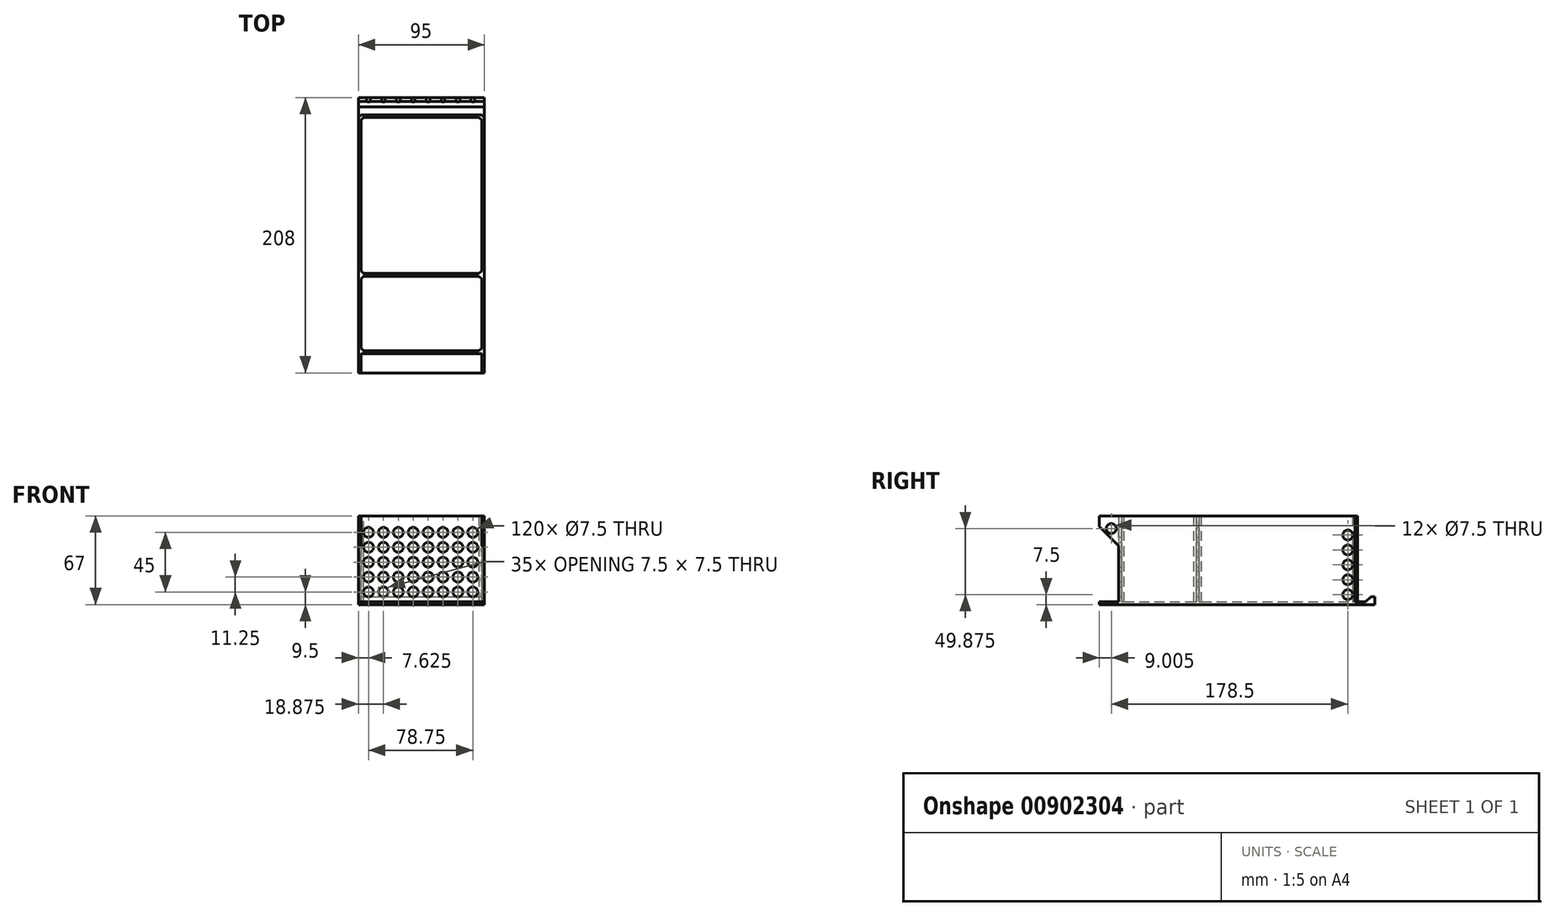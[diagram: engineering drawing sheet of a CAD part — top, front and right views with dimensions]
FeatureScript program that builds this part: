
annotation { "Feature Type Name" : "Feature", "Feature Type Description" : "" }
export const myFeature = defineFeature(function(context is Context, id is Id, definition is map)
    precondition{}
    {
        {
            assignVariable(context, id + "F0", {"name" : "d", "anyValue" : 67});
        }
        {
            assignVariable(context, id + "F1", {"name" : "noz", "anyValue" : .5});
        }
        {
            assignVariable(context, id + "F2", {"name" : "shell", "anyValue" : 2});
        }
        {
            assignVariable(context, id + "F3", {"name" : "wall", "anyValue" : getVariable(context, 'noz') * getVariable(context, 'shell') * 2});
        }
        {
            var Q0;
            Q0=qCreatedBy(makeId("Top.planeOp"),FACE);
            var sketch = newSketch(context, id + "F4", { "sketchPlane" : qUnion([Q0])});
            skLineSegment(sketch, "E0.bottom", {"start": v(0, 174.82) * mm, "end": v(47.5, 174.82) * mm});
            skLineSegment(sketch, "E0.top", {"start": v(0, -11.82) * mm, "end": v(45.5, -11.82) * mm});
            skLineSegment(sketch, "E0.left", {"start": v(0, 172.82) * mm, "end": v(0, -11.82) * mm});
            skLineSegment(sketch, "E0.right", {"start": v(47.5, 174.82) * mm, "end": v(47.5, -11.82) * mm});
            skLineSegment(sketch, "E1", {"start": v(45.5, 172.82) * mm, "end": v(45.5, 54.95) * mm});
            skLineSegment(sketch, "E2.top", {"start": v(47.5, -20.18) * mm, "end": v(45.5, -20.18) * mm});
            skLineSegment(sketch, "E2.left", {"start": v(47.5, -11.82) * mm, "end": v(47.5, -20.18) * mm});
            skLineSegment(sketch, "E2.right", {"start": v(45.5, -5.55) * mm, "end": v(45.5, -20.18) * mm});
            skLineSegment(sketch, "E3.bottom", {"start": v(0, -3.55) * mm, "end": v(45.5, -3.55) * mm});
            skLineSegment(sketch, "E3.top", {"start": v(0, -5.55) * mm, "end": v(45.5, -5.55) * mm});
            skLineSegment(sketch, "E3.left", {"start": v(0, -3.55) * mm, "end": v(0, -5.55) * mm});
            skLineSegment(sketch, "E4.bottom", {"start": v(0, 54.95) * mm, "end": v(45.5, 54.95) * mm});
            skLineSegment(sketch, "E4.top", {"start": v(0, 52.95) * mm, "end": v(45.5, 52.95) * mm});
            skLineSegment(sketch, "E4.left", {"start": v(0, 54.95) * mm, "end": v(0, 52.95) * mm});
            skLineSegment(sketch, "E5.bottom", {"start": v(0, 174.82) * mm, "end": v(48, 174.82) * mm});
            skLineSegment(sketch, "E5.top", {"start": v(0, 172.82) * mm, "end": v(45.5, 172.82) * mm});
            skLineSegment(sketch, "E6.MirrorCS", {"start": v(0, -11.82) * mm, "end": v(-45.5, -11.82) * mm});
            skLineSegment(sketch, "E7.MirrorCS", {"start": v(-47.5, -11.82) * mm, "end": v(-47.5, -20.18) * mm});
            skLineSegment(sketch, "E8.MirrorCS", {"start": v(0, 174.82) * mm, "end": v(-47.5, 174.82) * mm});
            skLineSegment(sketch, "E9.MirrorCS", {"start": v(0, 174.82) * mm, "end": v(-48, 174.82) * mm});
            skLineSegment(sketch, "E10.MirrorCS", {"start": v(-45.5, 172.82) * mm, "end": v(-45.5, 54.95) * mm});
            skLineSegment(sketch, "E11.MirrorCS", {"start": v(-45.5, -5.55) * mm, "end": v(-45.5, -20.18) * mm});
            skLineSegment(sketch, "E12.MirrorCS", {"start": v(0, 172.82) * mm, "end": v(-45.5, 172.82) * mm});
            skLineSegment(sketch, "E13.MirrorCS", {"start": v(-47.5, -20.18) * mm, "end": v(-45.5, -20.18) * mm});
            skLineSegment(sketch, "E14.MirrorCS", {"start": v(0, -3.55) * mm, "end": v(-45.5, -3.55) * mm});
            skLineSegment(sketch, "E15.MirrorCS", {"start": v(0, -5.55) * mm, "end": v(-45.5, -5.55) * mm});
            skLineSegment(sketch, "E16.MirrorCS", {"start": v(-47.5, 174.82) * mm, "end": v(-47.5, -11.82) * mm});
            skLineSegment(sketch, "E17.MirrorCS", {"start": v(0, 54.95) * mm, "end": v(-45.5, 54.95) * mm});
            skLineSegment(sketch, "E18.MirrorCS", {"start": v(0, 52.95) * mm, "end": v(-45.5, 52.95) * mm});
            skPoint(sketch, "E19.orphan", {"position": v(-45.5, 174.82) * mm});
            skPoint(sketch, "E20.orphan", {"position": v(45.5, 174.82) * mm});
            skLineSegment(sketch, "E21.trimOffspring", {"start": v(45.5, 52.95) * mm, "end": v(45.5, -3.55) * mm});
            skLineSegment(sketch, "E22.trimOffspring", {"start": v(-45.5, 52.95) * mm, "end": v(-45.5, -3.55) * mm});
            skPoint(sketch, "E23.orphan", {"position": v(-45.5, -11.82) * mm});
            skPoint(sketch, "E24.orphan", {"position": v(45.5, -11.82) * mm});
            skLineSegment(sketch, "E25", {"start": v(48.56, -20.18) * mm, "end": v(-45.5, -20.18) * mm});
            skLineSegment(sketch, "E26.bottom", {"start": v(-47.5, 174.82) * mm, "end": v(47.5, 174.82) * mm});
            skLineSegment(sketch, "E26.top", {"start": v(-47.5, 187.82) * mm, "end": v(47.5, 187.82) * mm});
            skLineSegment(sketch, "E26.left", {"start": v(-47.5, 174.82) * mm, "end": v(-47.5, 187.82) * mm});
            skLineSegment(sketch, "E26.right", {"start": v(47.5, 174.82) * mm, "end": v(47.5, 187.82) * mm});
            skLineSegment(sketch, "E27", {"start": v(-47.5, 185.82) * mm, "end": v(47.5, 185.82) * mm});
            skLineSegment(sketch, "E28.bottom", {"start": v(-45.5, 157.82) * mm, "end": v(45.5, 157.82) * mm});
            skLineSegment(sketch, "E28.top", {"start": v(-45.5, 155.82) * mm, "end": v(45.5, 155.82) * mm});
            skLineSegment(sketch, "E28.left", {"start": v(-45.5, 157.82) * mm, "end": v(-45.5, 155.82) * mm});
            skLineSegment(sketch, "E28.right", {"start": v(45.5, 157.82) * mm, "end": v(45.5, 155.82) * mm});
            skLineSegment(sketch, "E29.bottom", {"start": v(-45.5, 92.57) * mm, "end": v(45.5, 92.57) * mm});
            skLineSegment(sketch, "E29.top", {"start": v(-45.5, 90.57) * mm, "end": v(45.5, 90.57) * mm});
            skLineSegment(sketch, "E29.left", {"start": v(-45.5, 92.57) * mm, "end": v(-45.5, 90.57) * mm});
            skLineSegment(sketch, "E29.right", {"start": v(45.5, 92.57) * mm, "end": v(45.5, 90.57) * mm});
            skSolve(sketch);
        }
        {
            var Q0;
            Q0=makeQuery(id+"F4.imprint","IMPRINT",FACE,{"disambiguationData":[TD([[makeQuery(id+"F4.imprint","IMPRINT",EDGE,{"derivedFrom":sQuery(id+"F4.wireOp",EDGE,"E26.top")}),-1.0]])]});
            var Q1;
            {var subQ7=sQuery(id+"F4.wireOp",EDGE,"E0.right");Q1=makeQuery(id+"F4.imprint","IMPRINT",FACE,{"disambiguationData":[TD([[makeQuery(id+"F4.imprint","IMPRINT",EDGE,{"derivedFrom":subQ7}),-1.0]])]});}
            var Q2;
            Q2=makeQuery(id+"F4.imprint","IMPRINT",FACE,{"disambiguationData":[TD([[makeQuery(id+"F4.imprint","IMPRINT",EDGE,{"derivedFrom":sQuery(id+"F4.wireOp",EDGE,"E10.MirrorCS")}),1.0]])]});
            var Q3;
            Q3=makeQuery(id+"F4.imprint","IMPRINT",FACE,{"disambiguationData":[TD([[makeQuery(id+"F4.imprint","IMPRINT",EDGE,{"derivedFrom":sQuery(id+"F4.wireOp",EDGE,"E1")}),-1.0]])]});
            var Q4;
            {var subQ0=sQuery(id+"F4.wireOp",EDGE,"E3.bottom");Q4=makeQuery(id+"F4.imprint","IMPRINT",FACE,{"disambiguationData":[TD([[makeQuery(id+"F4.imprint","IMPRINT",EDGE,{"derivedFrom":subQ0}),1.0]])]});}
            var Q5;
            {var subQ0=sQuery(id+"F4.wireOp",EDGE,"E14.MirrorCS");Q5=makeQuery(id+"F4.imprint","IMPRINT",FACE,{"disambiguationData":[TD([[makeQuery(id+"F4.imprint","IMPRINT",EDGE,{"derivedFrom":subQ0}),-1.0]])]});}
            var Q6;
            {var subQ5=sQuery(id+"F4.wireOp",EDGE,"E0.top");Q6=makeQuery(id+"F4.imprint","IMPRINT",FACE,{"disambiguationData":[TD([[makeQuery(id+"F4.imprint","IMPRINT",EDGE,{"derivedFrom":subQ5}),-1.0]])]});}
            var Q7;
            {var subQ0=sQuery(id+"F4.wireOp",EDGE,"E0.top");Q7=makeQuery(id+"F4.imprint","IMPRINT",FACE,{"disambiguationData":[TD([[makeQuery(id+"F4.imprint","IMPRINT",EDGE,{"derivedFrom":subQ0}),1.0]])]});}
            var Q8;
            {var subQ0=sQuery(id+"F4.wireOp",EDGE,"E6.MirrorCS");Q8=makeQuery(id+"F4.imprint","IMPRINT",FACE,{"disambiguationData":[TD([[makeQuery(id+"F4.imprint","IMPRINT",EDGE,{"derivedFrom":subQ0}),-1.0]])]});}
            var Q9;
            {var subQ3=sQuery(id+"F4.wireOp",EDGE,"E27");Q9=makeQuery(id+"F4.imprint","IMPRINT",FACE,{"disambiguationData":[TD([[makeQuery(id+"F4.imprint","IMPRINT",EDGE,{"derivedFrom":subQ3}),-1.0]])]});}
            var Q10;
            Q10=makeQuery(id+"F4.imprint","IMPRINT",FACE,{"disambiguationData":[TD([[makeQuery(id+"F4.imprint","IMPRINT",EDGE,{"derivedFrom":sQuery(id+"F4.wireOp",EDGE,"E7.MirrorCS")}),1.0]])]});
            var Q11;
            {var subQ0=sQuery(id+"F4.wireOp",EDGE,"b3370406-a8f8-48eb-b0d9-f35a15d98687.0.1.16");var subQ1=sQuery(id+"F4.wireOp",EDGE,"E12.MirrorCS");var subQ2=makeQuery(id+"F4.imprint","INTERSECT",VERTEX,{"disambiguationData":[OD(1.0)],"derivedFrom":[subQ1,subQ0]});Q11=makeQuery(id+"F4.imprint","IMPRINT",FACE,{"disambiguationData":[TD([[makeQuery(id+"F4.imprint","IMPRINT",EDGE,{"disambiguationData":[TD([[subQ2,-1.0]])],"derivedFrom":subQ1}),-1.0]])]});}
            var Q12;
            {var subQ0=sQuery(id+"F4.wireOp",EDGE,"b3370406-a8f8-48eb-b0d9-f35a15d98687.0.2.16");var subQ1=sQuery(id+"F4.wireOp",EDGE,"E12.MirrorCS");var subQ2=makeQuery(id+"F4.imprint","INTERSECT",VERTEX,{"disambiguationData":[OD(1.0)],"derivedFrom":[subQ1,subQ0]});Q12=makeQuery(id+"F4.imprint","IMPRINT",FACE,{"disambiguationData":[TD([[makeQuery(id+"F4.imprint","IMPRINT",EDGE,{"disambiguationData":[TD([[subQ2,-1.0]])],"derivedFrom":subQ1}),-1.0]])]});}
            var Q13;
            {var subQ0=sQuery(id+"F4.wireOp",EDGE,"b3370406-a8f8-48eb-b0d9-f35a15d98687.0.2.16");var subQ1=sQuery(id+"F4.wireOp",EDGE,"E26.bottom");var subQ2=makeQuery(id+"F4.imprint","INTERSECT",VERTEX,{"disambiguationData":[OD(1.0)],"derivedFrom":[subQ1,subQ0]});Q13=makeQuery(id+"F4.imprint","IMPRINT",FACE,{"disambiguationData":[TD([[makeQuery(id+"F4.imprint","IMPRINT",EDGE,{"disambiguationData":[TD([[subQ2,-1.0]])],"derivedFrom":subQ1}),-1.0]])]});}
            var Q14;
            {var subQ0=sQuery(id+"F4.wireOp",EDGE,"b3370406-a8f8-48eb-b0d9-f35a15d98687.0.3.16");var subQ1=sQuery(id+"F4.wireOp",EDGE,"E5.top");var subQ2=makeQuery(id+"F4.imprint","INTERSECT",VERTEX,{"disambiguationData":[OD(1.0)],"derivedFrom":[subQ1,subQ0]});Q14=makeQuery(id+"F4.imprint","IMPRINT",FACE,{"disambiguationData":[TD([[makeQuery(id+"F4.imprint","IMPRINT",EDGE,{"disambiguationData":[TD([[subQ2,-1.0]])],"derivedFrom":subQ1}),1.0]])]});}
            var Q15;
            {var subQ0=sQuery(id+"F4.wireOp",EDGE,"b3370406-a8f8-48eb-b0d9-f35a15d98687.0.4.16");var subQ1=sQuery(id+"F4.wireOp",EDGE,"E5.top");var subQ2=makeQuery(id+"F4.imprint","INTERSECT",VERTEX,{"disambiguationData":[OD(1.0)],"derivedFrom":[subQ1,subQ0]});Q15=makeQuery(id+"F4.imprint","IMPRINT",FACE,{"disambiguationData":[TD([[makeQuery(id+"F4.imprint","IMPRINT",EDGE,{"disambiguationData":[TD([[subQ2,-1.0]])],"derivedFrom":subQ1}),1.0]])]});}
            var Q16;
            {var subQ5=sQuery(id+"F4.wireOp",EDGE,"E28.left");Q16=makeQuery(id+"F4.imprint","IMPRINT",FACE,{"disambiguationData":[TD([[makeQuery(id+"F4.imprint","IMPRINT",EDGE,{"derivedFrom":subQ5}),1.0]])]});}
            var Q17;
            {var subQ5=sQuery(id+"F4.wireOp",EDGE,"E28.right");Q17=makeQuery(id+"F4.imprint","IMPRINT",FACE,{"disambiguationData":[TD([[makeQuery(id+"F4.imprint","IMPRINT",EDGE,{"derivedFrom":subQ5}),-1.0]])]});}
            var Q18;
            {var subQ5=sQuery(id+"F4.wireOp",EDGE,"E29.left");Q18=makeQuery(id+"F4.imprint","IMPRINT",FACE,{"disambiguationData":[TD([[makeQuery(id+"F4.imprint","IMPRINT",EDGE,{"derivedFrom":subQ5}),1.0]])]});}
            var Q19;
            {var subQ5=sQuery(id+"F4.wireOp",EDGE,"E29.right");Q19=makeQuery(id+"F4.imprint","IMPRINT",FACE,{"disambiguationData":[TD([[makeQuery(id+"F4.imprint","IMPRINT",EDGE,{"derivedFrom":subQ5}),-1.0]])]});}
            extrude(context, id + "F5", {"entities" : qUnion([Q0, Q1, Q2, Q3, Q4, Q5, Q6, Q7, Q8, Q9, Q10, Q11, Q12, Q13, Q14, Q15, Q16, Q17, Q18, Q19]), "depth" : (getVariable(context, 'wall')) * mm, "offsetDistance" : 25 * mm});
        }
        {
            var Q0;
            {var subQ7=sQuery(id+"F4.wireOp",EDGE,"E0.right");Q0=makeQuery(id+"F4.imprint","IMPRINT",FACE,{"disambiguationData":[TD([[makeQuery(id+"F4.imprint","IMPRINT",EDGE,{"derivedFrom":subQ7}),-1.0]])]});}
            var Q1;
            {var subQ0=sQuery(id+"F4.wireOp",EDGE,"b3370406-a8f8-48eb-b0d9-f35a15d98687.0.2.16");var subQ3=sQuery(id+"F4.wireOp",EDGE,"E26.bottom");var subQ4=makeQuery(id+"F4.imprint","INTERSECT",VERTEX,{"disambiguationData":[OD(1.0)],"derivedFrom":[subQ3,subQ0]});Q1=makeQuery(id+"F4.imprint","IMPRINT",FACE,{"disambiguationData":[TD([[makeQuery(id+"F4.imprint","IMPRINT",EDGE,{"disambiguationData":[TD([[subQ4,-1.0]])],"derivedFrom":subQ3}),-1.0]])]});}
            var Q2;
            {var subQ0=sQuery(id+"F4.wireOp",EDGE,"b3370406-a8f8-48eb-b0d9-f35a15d98687.0.2.16");var subQ1=sQuery(id+"F4.wireOp",EDGE,"E12.MirrorCS");var subQ2=makeQuery(id+"F4.imprint","INTERSECT",VERTEX,{"disambiguationData":[OD(0.0)],"derivedFrom":[subQ1,subQ0]});Q2=makeQuery(id+"F4.imprint","IMPRINT",FACE,{"disambiguationData":[TD([[makeQuery(id+"F4.imprint","IMPRINT",EDGE,{"disambiguationData":[TD([[subQ2,-1.0]])],"derivedFrom":subQ1}),-1.0]])]});}
            var Q3;
            {var subQ0=sQuery(id+"F4.wireOp",EDGE,"b3370406-a8f8-48eb-b0d9-f35a15d98687.0.2.16");var subQ1=sQuery(id+"F4.wireOp",EDGE,"E12.MirrorCS");var subQ2=makeQuery(id+"F4.imprint","INTERSECT",VERTEX,{"disambiguationData":[OD(1.0)],"derivedFrom":[subQ1,subQ0]});Q3=makeQuery(id+"F4.imprint","IMPRINT",FACE,{"disambiguationData":[TD([[makeQuery(id+"F4.imprint","IMPRINT",EDGE,{"disambiguationData":[TD([[subQ2,-1.0]])],"derivedFrom":subQ1}),-1.0]])]});}
            var Q4;
            {var subQ0=sQuery(id+"F4.wireOp",EDGE,"b3370406-a8f8-48eb-b0d9-f35a15d98687.0.1.16");var subQ1=sQuery(id+"F4.wireOp",EDGE,"E12.MirrorCS");var subQ2=makeQuery(id+"F4.imprint","INTERSECT",VERTEX,{"disambiguationData":[OD(0.0)],"derivedFrom":[subQ1,subQ0]});Q4=makeQuery(id+"F4.imprint","IMPRINT",FACE,{"disambiguationData":[TD([[makeQuery(id+"F4.imprint","IMPRINT",EDGE,{"disambiguationData":[TD([[subQ2,-1.0]])],"derivedFrom":subQ1}),-1.0]])]});}
            var Q5;
            {var subQ0=sQuery(id+"F4.wireOp",EDGE,"b3370406-a8f8-48eb-b0d9-f35a15d98687.0.0.16");var subQ1=sQuery(id+"F4.wireOp",EDGE,"E12.MirrorCS");var subQ2=makeQuery(id+"F4.imprint","INTERSECT",VERTEX,{"disambiguationData":[OD(0.0)],"derivedFrom":[subQ1,subQ0]});Q5=makeQuery(id+"F4.imprint","IMPRINT",FACE,{"disambiguationData":[TD([[makeQuery(id+"F4.imprint","IMPRINT",EDGE,{"disambiguationData":[TD([[subQ2,-1.0]])],"derivedFrom":subQ1}),-1.0]])]});}
            var Q6;
            {var subQ0=sQuery(id+"F4.wireOp",EDGE,"b3370406-a8f8-48eb-b0d9-f35a15d98687.0.1.16");var subQ1=sQuery(id+"F4.wireOp",EDGE,"E12.MirrorCS");var subQ2=makeQuery(id+"F4.imprint","INTERSECT",VERTEX,{"disambiguationData":[OD(1.0)],"derivedFrom":[subQ1,subQ0]});Q6=makeQuery(id+"F4.imprint","IMPRINT",FACE,{"disambiguationData":[TD([[makeQuery(id+"F4.imprint","IMPRINT",EDGE,{"disambiguationData":[TD([[subQ2,-1.0]])],"derivedFrom":subQ1}),-1.0]])]});}
            var Q7;
            {var subQ0=sQuery(id+"F4.wireOp",EDGE,"b3370406-a8f8-48eb-b0d9-f35a15d98687.0.3.16");var subQ1=sQuery(id+"F4.wireOp",EDGE,"E5.top");var subQ2=makeQuery(id+"F4.imprint","INTERSECT",VERTEX,{"disambiguationData":[OD(0.0)],"derivedFrom":[subQ1,subQ0]});Q7=makeQuery(id+"F4.imprint","IMPRINT",FACE,{"disambiguationData":[TD([[makeQuery(id+"F4.imprint","IMPRINT",EDGE,{"disambiguationData":[TD([[subQ2,-1.0]])],"derivedFrom":subQ1}),1.0]])]});}
            var Q8;
            {var subQ0=sQuery(id+"F4.wireOp",EDGE,"b3370406-a8f8-48eb-b0d9-f35a15d98687.0.3.16");var subQ1=sQuery(id+"F4.wireOp",EDGE,"E5.top");var subQ2=makeQuery(id+"F4.imprint","INTERSECT",VERTEX,{"disambiguationData":[OD(1.0)],"derivedFrom":[subQ1,subQ0]});Q8=makeQuery(id+"F4.imprint","IMPRINT",FACE,{"disambiguationData":[TD([[makeQuery(id+"F4.imprint","IMPRINT",EDGE,{"disambiguationData":[TD([[subQ2,-1.0]])],"derivedFrom":subQ1}),1.0]])]});}
            var Q9;
            {var subQ0=sQuery(id+"F4.wireOp",EDGE,"b3370406-a8f8-48eb-b0d9-f35a15d98687.0.4.16");var subQ1=sQuery(id+"F4.wireOp",EDGE,"E5.top");var subQ2=makeQuery(id+"F4.imprint","INTERSECT",VERTEX,{"disambiguationData":[OD(0.0)],"derivedFrom":[subQ1,subQ0]});Q9=makeQuery(id+"F4.imprint","IMPRINT",FACE,{"disambiguationData":[TD([[makeQuery(id+"F4.imprint","IMPRINT",EDGE,{"disambiguationData":[TD([[subQ2,-1.0]])],"derivedFrom":subQ1}),1.0]])]});}
            var Q10;
            {var subQ0=sQuery(id+"F4.wireOp",EDGE,"b3370406-a8f8-48eb-b0d9-f35a15d98687.0.4.16");var subQ1=sQuery(id+"F4.wireOp",EDGE,"E5.top");var subQ2=makeQuery(id+"F4.imprint","INTERSECT",VERTEX,{"disambiguationData":[OD(1.0)],"derivedFrom":[subQ1,subQ0]});Q10=makeQuery(id+"F4.imprint","IMPRINT",FACE,{"disambiguationData":[TD([[makeQuery(id+"F4.imprint","IMPRINT",EDGE,{"disambiguationData":[TD([[subQ2,-1.0]])],"derivedFrom":subQ1}),1.0]])]});}
            var Q11;
            {var subQ0=sQuery(id+"F4.wireOp",EDGE,"b3370406-a8f8-48eb-b0d9-f35a15d98687.0.5.16");var subQ1=sQuery(id+"F4.wireOp",EDGE,"E5.top");var subQ2=makeQuery(id+"F4.imprint","INTERSECT",VERTEX,{"disambiguationData":[OD(0.0)],"derivedFrom":[subQ1,subQ0]});Q11=makeQuery(id+"F4.imprint","IMPRINT",FACE,{"disambiguationData":[TD([[makeQuery(id+"F4.imprint","IMPRINT",EDGE,{"disambiguationData":[TD([[subQ2,-1.0]])],"derivedFrom":subQ1}),1.0]])]});}
            var Q12;
            {var subQ0=sQuery(id+"F4.wireOp",EDGE,"913f8327-6014-45d2-8669-990423f078e8.3.6.0");var subQ1=sQuery(id+"F4.wireOp",EDGE,"E4.bottom");var subQ2=makeQuery(id+"F4.imprint","INTERSECT",VERTEX,{"disambiguationData":[OD(0.0)],"derivedFrom":[subQ1,subQ0]});Q12=makeQuery(id+"F4.imprint","IMPRINT",FACE,{"disambiguationData":[TD([[makeQuery(id+"F4.imprint","IMPRINT",EDGE,{"disambiguationData":[TD([[subQ2,-1.0]])],"derivedFrom":subQ1}),-1.0]])]});}
            var Q13;
            {var subQ0=sQuery(id+"F4.wireOp",EDGE,"913f8327-6014-45d2-8669-990423f078e8.2.6.0");var subQ1=sQuery(id+"F4.wireOp",EDGE,"E17.MirrorCS");var subQ2=makeQuery(id+"F4.imprint","INTERSECT",VERTEX,{"disambiguationData":[OD(0.0)],"derivedFrom":[subQ1,subQ0]});Q13=makeQuery(id+"F4.imprint","IMPRINT",FACE,{"disambiguationData":[TD([[makeQuery(id+"F4.imprint","IMPRINT",EDGE,{"disambiguationData":[TD([[subQ2,-1.0]])],"derivedFrom":subQ1}),1.0]])]});}
            var Q14;
            {var subQ0=sQuery(id+"F4.wireOp",EDGE,"913f8327-6014-45d2-8669-990423f078e8.1.6.0");var subQ1=sQuery(id+"F4.wireOp",EDGE,"E17.MirrorCS");var subQ2=makeQuery(id+"F4.imprint","INTERSECT",VERTEX,{"disambiguationData":[OD(0.0)],"derivedFrom":[subQ1,subQ0]});Q14=makeQuery(id+"F4.imprint","IMPRINT",FACE,{"disambiguationData":[TD([[makeQuery(id+"F4.imprint","IMPRINT",EDGE,{"disambiguationData":[TD([[subQ2,-1.0]])],"derivedFrom":subQ1}),1.0]])]});}
            var Q15;
            {var subQ0=sQuery(id+"F4.wireOp",EDGE,"913f8327-6014-45d2-8669-990423f078e8.0.6.0");var subQ1=sQuery(id+"F4.wireOp",EDGE,"E17.MirrorCS");var subQ2=makeQuery(id+"F4.imprint","INTERSECT",VERTEX,{"disambiguationData":[OD(0.0)],"derivedFrom":[subQ1,subQ0]});Q15=makeQuery(id+"F4.imprint","IMPRINT",FACE,{"disambiguationData":[TD([[makeQuery(id+"F4.imprint","IMPRINT",EDGE,{"disambiguationData":[TD([[subQ2,-1.0]])],"derivedFrom":subQ1}),1.0]])]});}
            var Q16;
            Q16=makeQuery(id+"F4.imprint","IMPRINT",FACE,{"disambiguationData":[TD([[makeQuery(id+"F4.imprint","IMPRINT",EDGE,{"derivedFrom":sQuery(id+"F4.wireOp",EDGE,"E7.MirrorCS")}),1.0]])]});
            var Q17;
            {var subQ0=sQuery(id+"F4.wireOp",EDGE,"913f8327-6014-45d2-8669-990423f078e8.4.6.0");var subQ1=sQuery(id+"F4.wireOp",EDGE,"E4.bottom");var subQ2=makeQuery(id+"F4.imprint","INTERSECT",VERTEX,{"disambiguationData":[OD(0.0)],"derivedFrom":[subQ1,subQ0]});Q17=makeQuery(id+"F4.imprint","IMPRINT",FACE,{"disambiguationData":[TD([[makeQuery(id+"F4.imprint","IMPRINT",EDGE,{"disambiguationData":[TD([[subQ2,-1.0]])],"derivedFrom":subQ1}),-1.0]])]});}
            var Q18;
            {var subQ0=sQuery(id+"F4.wireOp",EDGE,"913f8327-6014-45d2-8669-990423f078e8.5.6.0");var subQ1=sQuery(id+"F4.wireOp",EDGE,"E4.bottom");var subQ2=makeQuery(id+"F4.imprint","INTERSECT",VERTEX,{"disambiguationData":[OD(0.0)],"derivedFrom":[subQ1,subQ0]});Q18=makeQuery(id+"F4.imprint","IMPRINT",FACE,{"disambiguationData":[TD([[makeQuery(id+"F4.imprint","IMPRINT",EDGE,{"disambiguationData":[TD([[subQ2,-1.0]])],"derivedFrom":subQ1}),-1.0]])]});}
            var Q19;
            {var subQ0=sQuery(id+"F4.wireOp",EDGE,"913f8327-6014-45d2-8669-990423f078e8.0.1.0");var subQ1=sQuery(id+"F4.wireOp",EDGE,"E14.MirrorCS");var subQ2=makeQuery(id+"F4.imprint","INTERSECT",VERTEX,{"disambiguationData":[OD(0.0)],"derivedFrom":[subQ1,subQ0]});Q19=makeQuery(id+"F4.imprint","IMPRINT",FACE,{"disambiguationData":[TD([[makeQuery(id+"F4.imprint","IMPRINT",EDGE,{"disambiguationData":[TD([[subQ2,-1.0]])],"derivedFrom":subQ1}),1.0]])]});}
            var Q20;
            {var subQ0=sQuery(id+"F4.wireOp",EDGE,"913f8327-6014-45d2-8669-990423f078e8.1.1.0");var subQ1=sQuery(id+"F4.wireOp",EDGE,"E14.MirrorCS");var subQ2=makeQuery(id+"F4.imprint","INTERSECT",VERTEX,{"disambiguationData":[OD(0.0)],"derivedFrom":[subQ1,subQ0]});Q20=makeQuery(id+"F4.imprint","IMPRINT",FACE,{"disambiguationData":[TD([[makeQuery(id+"F4.imprint","IMPRINT",EDGE,{"disambiguationData":[TD([[subQ2,-1.0]])],"derivedFrom":subQ1}),1.0]])]});}
            var Q21;
            {var subQ0=sQuery(id+"F4.wireOp",EDGE,"913f8327-6014-45d2-8669-990423f078e8.2.1.0");var subQ1=sQuery(id+"F4.wireOp",EDGE,"E14.MirrorCS");var subQ2=makeQuery(id+"F4.imprint","INTERSECT",VERTEX,{"disambiguationData":[OD(0.0)],"derivedFrom":[subQ1,subQ0]});Q21=makeQuery(id+"F4.imprint","IMPRINT",FACE,{"disambiguationData":[TD([[makeQuery(id+"F4.imprint","IMPRINT",EDGE,{"disambiguationData":[TD([[subQ2,-1.0]])],"derivedFrom":subQ1}),1.0]])]});}
            var Q22;
            {var subQ0=sQuery(id+"F4.wireOp",EDGE,"913f8327-6014-45d2-8669-990423f078e8.3.1.0");var subQ1=sQuery(id+"F4.wireOp",EDGE,"E3.bottom");var subQ2=makeQuery(id+"F4.imprint","INTERSECT",VERTEX,{"disambiguationData":[OD(0.0)],"derivedFrom":[subQ1,subQ0]});Q22=makeQuery(id+"F4.imprint","IMPRINT",FACE,{"disambiguationData":[TD([[makeQuery(id+"F4.imprint","IMPRINT",EDGE,{"disambiguationData":[TD([[subQ2,-1.0]])],"derivedFrom":subQ1}),-1.0]])]});}
            var Q23;
            {var subQ0=sQuery(id+"F4.wireOp",EDGE,"913f8327-6014-45d2-8669-990423f078e8.4.1.0");var subQ1=sQuery(id+"F4.wireOp",EDGE,"E3.bottom");var subQ2=makeQuery(id+"F4.imprint","INTERSECT",VERTEX,{"disambiguationData":[OD(0.0)],"derivedFrom":[subQ1,subQ0]});Q23=makeQuery(id+"F4.imprint","IMPRINT",FACE,{"disambiguationData":[TD([[makeQuery(id+"F4.imprint","IMPRINT",EDGE,{"disambiguationData":[TD([[subQ2,-1.0]])],"derivedFrom":subQ1}),-1.0]])]});}
            var Q24;
            {var subQ0=sQuery(id+"F4.wireOp",EDGE,"913f8327-6014-45d2-8669-990423f078e8.5.1.0");var subQ1=sQuery(id+"F4.wireOp",EDGE,"E3.bottom");var subQ2=makeQuery(id+"F4.imprint","INTERSECT",VERTEX,{"disambiguationData":[OD(0.0)],"derivedFrom":[subQ1,subQ0]});Q24=makeQuery(id+"F4.imprint","IMPRINT",FACE,{"disambiguationData":[TD([[makeQuery(id+"F4.imprint","IMPRINT",EDGE,{"disambiguationData":[TD([[subQ2,-1.0]])],"derivedFrom":subQ1}),-1.0]])]});}
            var Q25;
            {var subQ5=sQuery(id+"F4.wireOp",EDGE,"E28.right");Q25=makeQuery(id+"F4.imprint","IMPRINT",FACE,{"disambiguationData":[TD([[makeQuery(id+"F4.imprint","IMPRINT",EDGE,{"derivedFrom":subQ5}),-1.0]])]});}
            var Q26;
            {var subQ5=sQuery(id+"F4.wireOp",EDGE,"E28.left");Q26=makeQuery(id+"F4.imprint","IMPRINT",FACE,{"disambiguationData":[TD([[makeQuery(id+"F4.imprint","IMPRINT",EDGE,{"derivedFrom":subQ5}),1.0]])]});}
            var Q27;
            {var subQ5=sQuery(id+"F4.wireOp",EDGE,"E29.right");Q27=makeQuery(id+"F4.imprint","IMPRINT",FACE,{"disambiguationData":[TD([[makeQuery(id+"F4.imprint","IMPRINT",EDGE,{"derivedFrom":subQ5}),-1.0]])]});}
            var Q28;
            {var subQ5=sQuery(id+"F4.wireOp",EDGE,"E29.left");Q28=makeQuery(id+"F4.imprint","IMPRINT",FACE,{"disambiguationData":[TD([[makeQuery(id+"F4.imprint","IMPRINT",EDGE,{"derivedFrom":subQ5}),1.0]])]});}
            extrude(context, id + "F6", {"entities" : qUnion([Q0, Q1, Q2, Q3, Q4, Q5, Q6, Q7, Q8, Q9, Q10, Q11, Q12, Q13, Q14, Q15, Q16, Q17, Q18, Q19, Q20, Q21, Q22, Q23, Q24, Q25, Q26, Q27, Q28]), "operationType" : NewBodyOperationType.ADD, "depth" : (getVariable(context, 'd')) * mm, "offsetDistance" : 25 * mm});
        }
        {
            var Q0;
            {var subQ0=sQuery(id+"F4.wireOp",EDGE,"E26.top");Q0=makeQuery(id+"F4.imprint","IMPRINT",FACE,{"disambiguationData":[TD([[makeQuery(id+"F4.imprint","IMPRINT",EDGE,{"derivedFrom":subQ0}),-1.0]])]});}
            extrude(context, id + "F7", {"entities" : qUnion([Q0]), "operationType" : NewBodyOperationType.ADD, "depth" : (getVariable(context, 'wall') * 3) * mm, "offsetDistance" : 25 * mm});
        }
        {
            var Q0;
            {var subQ0=sQuery(id+"F4.wireOp",EDGE,"b3370406-a8f8-48eb-b0d9-f35a15d98687.0.5.16");var subQ1=sQuery(id+"F4.wireOp",EDGE,"b3370406-a8f8-48eb-b0d9-f35a15d98687.0.3.16");var subQ2=sQuery(id+"F4.wireOp",EDGE,"E26.left");var subQ3=sQuery(id+"F4.wireOp",EDGE,"E16.MirrorCS");var subQ4=sQuery(id+"F4.wireOp",EDGE,"E7.MirrorCS");var subQ5=sQuery(id+"F4.wireOp",EDGE,"b3370406-a8f8-48eb-b0d9-f35a15d98687.0.2.16");var subQ6=sQuery(id+"F4.wireOp",EDGE,"E2.left");var subQ7=sQuery(id+"F4.wireOp",EDGE,"E0.right");var subQ8=sQuery(id+"F4.wireOp",EDGE,"b3370406-a8f8-48eb-b0d9-f35a15d98687.0.1.16");var subQ9=sQuery(id+"F4.wireOp",EDGE,"b3370406-a8f8-48eb-b0d9-f35a15d98687.0.4.16");var subQ10=sQuery(id+"F4.wireOp",EDGE,"E26.right");var subQ11=sQuery(id+"F4.wireOp",EDGE,"b3370406-a8f8-48eb-b0d9-f35a15d98687.0.0.16");var subQ12=sQuery(id+"F4.wireOp",EDGE,"E26.top");Q0=makeQuery(id+"F7.boolean.opBoolean","INTERSECT",EDGE,{"derivedFrom":[makeQuery(id+"F6.boolean.opBoolean","SPLIT",FACE,{"disambiguationData":[TD([makeQuery(id+"F5.opExtrude","SWEPT_FACE",FACE,{"disambiguationData":[OSD([subQ12])]})])],"derivedFrom":makeQuery(id+"F5.opExtrude","CAP_FACE",FACE,{"disambiguationData":[OSD([subQ7,subQ6,subQ4,sQuery(id+"F4.wireOp",EDGE,"E13.MirrorCS"),subQ3,sQuery(id+"F4.wireOp",EDGE,"E25"),subQ12,subQ2,subQ10,sQuery(id+"F4.wireOp",EDGE,"qAj5cU3M-lTBo-jIVI-jIF2-Nz4z5NPNRST0"),sQuery(id+"F4.wireOp",EDGE,"913f8327-6014-45d2-8669-990423f078e8.0.1.0"),sQuery(id+"F4.wireOp",EDGE,"913f8327-6014-45d2-8669-990423f078e8.0.2.0"),sQuery(id+"F4.wireOp",EDGE,"913f8327-6014-45d2-8669-990423f078e8.0.3.0"),sQuery(id+"F4.wireOp",EDGE,"913f8327-6014-45d2-8669-990423f078e8.0.4.0"),sQuery(id+"F4.wireOp",EDGE,"913f8327-6014-45d2-8669-990423f078e8.0.5.0"),sQuery(id+"F4.wireOp",EDGE,"913f8327-6014-45d2-8669-990423f078e8.0.6.0"),sQuery(id+"F4.wireOp",EDGE,"913f8327-6014-45d2-8669-990423f078e8.0.7.0"),sQuery(id+"F4.wireOp",EDGE,"913f8327-6014-45d2-8669-990423f078e8.0.8.0"),sQuery(id+"F4.wireOp",EDGE,"913f8327-6014-45d2-8669-990423f078e8.0.9.0"),sQuery(id+"F4.wireOp",EDGE,"913f8327-6014-45d2-8669-990423f078e8.0.10.0"),sQuery(id+"F4.wireOp",EDGE,"913f8327-6014-45d2-8669-990423f078e8.1.0.0"),sQuery(id+"F4.wireOp",EDGE,"913f8327-6014-45d2-8669-990423f078e8.1.1.0"),sQuery(id+"F4.wireOp",EDGE,"913f8327-6014-45d2-8669-990423f078e8.1.2.0"),sQuery(id+"F4.wireOp",EDGE,"913f8327-6014-45d2-8669-990423f078e8.1.3.0"),sQuery(id+"F4.wireOp",EDGE,"913f8327-6014-45d2-8669-990423f078e8.1.4.0"),sQuery(id+"F4.wireOp",EDGE,"913f8327-6014-45d2-8669-990423f078e8.1.5.0"),sQuery(id+"F4.wireOp",EDGE,"913f8327-6014-45d2-8669-990423f078e8.1.6.0"),sQuery(id+"F4.wireOp",EDGE,"913f8327-6014-45d2-8669-990423f078e8.1.7.0"),sQuery(id+"F4.wireOp",EDGE,"913f8327-6014-45d2-8669-990423f078e8.1.8.0"),sQuery(id+"F4.wireOp",EDGE,"913f8327-6014-45d2-8669-990423f078e8.1.9.0"),sQuery(id+"F4.wireOp",EDGE,"913f8327-6014-45d2-8669-990423f078e8.1.10.0"),sQuery(id+"F4.wireOp",EDGE,"913f8327-6014-45d2-8669-990423f078e8.2.0.0"),sQuery(id+"F4.wireOp",EDGE,"913f8327-6014-45d2-8669-990423f078e8.2.1.0"),sQuery(id+"F4.wireOp",EDGE,"913f8327-6014-45d2-8669-990423f078e8.2.2.0"),sQuery(id+"F4.wireOp",EDGE,"913f8327-6014-45d2-8669-990423f078e8.2.3.0"),sQuery(id+"F4.wireOp",EDGE,"913f8327-6014-45d2-8669-990423f078e8.2.4.0"),sQuery(id+"F4.wireOp",EDGE,"913f8327-6014-45d2-8669-990423f078e8.2.5.0"),sQuery(id+"F4.wireOp",EDGE,"913f8327-6014-45d2-8669-990423f078e8.2.6.0"),sQuery(id+"F4.wireOp",EDGE,"913f8327-6014-45d2-8669-990423f078e8.2.7.0"),sQuery(id+"F4.wireOp",EDGE,"913f8327-6014-45d2-8669-990423f078e8.2.8.0"),sQuery(id+"F4.wireOp",EDGE,"913f8327-6014-45d2-8669-990423f078e8.2.9.0"),sQuery(id+"F4.wireOp",EDGE,"913f8327-6014-45d2-8669-990423f078e8.2.10.0"),sQuery(id+"F4.wireOp",EDGE,"913f8327-6014-45d2-8669-990423f078e8.3.0.0"),sQuery(id+"F4.wireOp",EDGE,"913f8327-6014-45d2-8669-990423f078e8.3.1.0"),sQuery(id+"F4.wireOp",EDGE,"913f8327-6014-45d2-8669-990423f078e8.3.2.0"),sQuery(id+"F4.wireOp",EDGE,"913f8327-6014-45d2-8669-990423f078e8.3.3.0"),sQuery(id+"F4.wireOp",EDGE,"913f8327-6014-45d2-8669-990423f078e8.3.4.0"),sQuery(id+"F4.wireOp",EDGE,"913f8327-6014-45d2-8669-990423f078e8.3.5.0"),sQuery(id+"F4.wireOp",EDGE,"913f8327-6014-45d2-8669-990423f078e8.3.6.0"),sQuery(id+"F4.wireOp",EDGE,"913f8327-6014-45d2-8669-990423f078e8.3.7.0"),sQuery(id+"F4.wireOp",EDGE,"913f8327-6014-45d2-8669-990423f078e8.3.8.0"),sQuery(id+"F4.wireOp",EDGE,"913f8327-6014-45d2-8669-990423f078e8.3.9.0"),sQuery(id+"F4.wireOp",EDGE,"913f8327-6014-45d2-8669-990423f078e8.3.10.0"),sQuery(id+"F4.wireOp",EDGE,"913f8327-6014-45d2-8669-990423f078e8.4.0.0"),sQuery(id+"F4.wireOp",EDGE,"913f8327-6014-45d2-8669-990423f078e8.4.1.0"),sQuery(id+"F4.wireOp",EDGE,"913f8327-6014-45d2-8669-990423f078e8.4.2.0"),sQuery(id+"F4.wireOp",EDGE,"913f8327-6014-45d2-8669-990423f078e8.4.3.0"),sQuery(id+"F4.wireOp",EDGE,"913f8327-6014-45d2-8669-990423f078e8.4.4.0"),sQuery(id+"F4.wireOp",EDGE,"913f8327-6014-45d2-8669-990423f078e8.4.5.0"),sQuery(id+"F4.wireOp",EDGE,"913f8327-6014-45d2-8669-990423f078e8.4.6.0"),sQuery(id+"F4.wireOp",EDGE,"913f8327-6014-45d2-8669-990423f078e8.4.7.0"),sQuery(id+"F4.wireOp",EDGE,"913f8327-6014-45d2-8669-990423f078e8.4.8.0"),sQuery(id+"F4.wireOp",EDGE,"913f8327-6014-45d2-8669-990423f078e8.4.9.0"),sQuery(id+"F4.wireOp",EDGE,"913f8327-6014-45d2-8669-990423f078e8.4.10.0"),sQuery(id+"F4.wireOp",EDGE,"913f8327-6014-45d2-8669-990423f078e8.5.0.0"),sQuery(id+"F4.wireOp",EDGE,"913f8327-6014-45d2-8669-990423f078e8.5.1.0"),sQuery(id+"F4.wireOp",EDGE,"913f8327-6014-45d2-8669-990423f078e8.5.2.0"),sQuery(id+"F4.wireOp",EDGE,"913f8327-6014-45d2-8669-990423f078e8.5.3.0"),sQuery(id+"F4.wireOp",EDGE,"913f8327-6014-45d2-8669-990423f078e8.5.4.0"),sQuery(id+"F4.wireOp",EDGE,"913f8327-6014-45d2-8669-990423f078e8.5.5.0"),sQuery(id+"F4.wireOp",EDGE,"913f8327-6014-45d2-8669-990423f078e8.5.6.0"),sQuery(id+"F4.wireOp",EDGE,"913f8327-6014-45d2-8669-990423f078e8.5.7.0"),sQuery(id+"F4.wireOp",EDGE,"913f8327-6014-45d2-8669-990423f078e8.5.8.0"),sQuery(id+"F4.wireOp",EDGE,"913f8327-6014-45d2-8669-990423f078e8.5.9.0"),sQuery(id+"F4.wireOp",EDGE,"913f8327-6014-45d2-8669-990423f078e8.5.10.0"),sQuery(id+"F4.wireOp",EDGE,"b3370406-a8f8-48eb-b0d9-f35a15d98687.0.0.11"),sQuery(id+"F4.wireOp",EDGE,"b3370406-a8f8-48eb-b0d9-f35a15d98687.0.0.12"),sQuery(id+"F4.wireOp",EDGE,"b3370406-a8f8-48eb-b0d9-f35a15d98687.0.0.13"),sQuery(id+"F4.wireOp",EDGE,"b3370406-a8f8-48eb-b0d9-f35a15d98687.0.0.14"),sQuery(id+"F4.wireOp",EDGE,"b3370406-a8f8-48eb-b0d9-f35a15d98687.0.0.15"),subQ11,sQuery(id+"F4.wireOp",EDGE,"b3370406-a8f8-48eb-b0d9-f35a15d98687.0.1.11"),sQuery(id+"F4.wireOp",EDGE,"b3370406-a8f8-48eb-b0d9-f35a15d98687.0.1.12"),sQuery(id+"F4.wireOp",EDGE,"b3370406-a8f8-48eb-b0d9-f35a15d98687.0.1.13"),sQuery(id+"F4.wireOp",EDGE,"b3370406-a8f8-48eb-b0d9-f35a15d98687.0.1.14"),sQuery(id+"F4.wireOp",EDGE,"b3370406-a8f8-48eb-b0d9-f35a15d98687.0.1.15"),subQ8,sQuery(id+"F4.wireOp",EDGE,"b3370406-a8f8-48eb-b0d9-f35a15d98687.0.2.11"),sQuery(id+"F4.wireOp",EDGE,"b3370406-a8f8-48eb-b0d9-f35a15d98687.0.2.12"),sQuery(id+"F4.wireOp",EDGE,"b3370406-a8f8-48eb-b0d9-f35a15d98687.0.2.13"),sQuery(id+"F4.wireOp",EDGE,"b3370406-a8f8-48eb-b0d9-f35a15d98687.0.2.14"),sQuery(id+"F4.wireOp",EDGE,"b3370406-a8f8-48eb-b0d9-f35a15d98687.0.2.15"),subQ5,sQuery(id+"F4.wireOp",EDGE,"b3370406-a8f8-48eb-b0d9-f35a15d98687.0.3.11"),sQuery(id+"F4.wireOp",EDGE,"b3370406-a8f8-48eb-b0d9-f35a15d98687.0.3.12"),sQuery(id+"F4.wireOp",EDGE,"b3370406-a8f8-48eb-b0d9-f35a15d98687.0.3.13"),sQuery(id+"F4.wireOp",EDGE,"b3370406-a8f8-48eb-b0d9-f35a15d98687.0.3.14"),sQuery(id+"F4.wireOp",EDGE,"b3370406-a8f8-48eb-b0d9-f35a15d98687.0.3.15"),subQ1,sQuery(id+"F4.wireOp",EDGE,"b3370406-a8f8-48eb-b0d9-f35a15d98687.0.4.11"),sQuery(id+"F4.wireOp",EDGE,"b3370406-a8f8-48eb-b0d9-f35a15d98687.0.4.12"),sQuery(id+"F4.wireOp",EDGE,"b3370406-a8f8-48eb-b0d9-f35a15d98687.0.4.13"),sQuery(id+"F4.wireOp",EDGE,"b3370406-a8f8-48eb-b0d9-f35a15d98687.0.4.14"),sQuery(id+"F4.wireOp",EDGE,"b3370406-a8f8-48eb-b0d9-f35a15d98687.0.4.15"),subQ9,sQuery(id+"F4.wireOp",EDGE,"b3370406-a8f8-48eb-b0d9-f35a15d98687.0.5.11"),sQuery(id+"F4.wireOp",EDGE,"b3370406-a8f8-48eb-b0d9-f35a15d98687.0.5.12"),sQuery(id+"F4.wireOp",EDGE,"b3370406-a8f8-48eb-b0d9-f35a15d98687.0.5.13"),sQuery(id+"F4.wireOp",EDGE,"b3370406-a8f8-48eb-b0d9-f35a15d98687.0.5.14"),sQuery(id+"F4.wireOp",EDGE,"b3370406-a8f8-48eb-b0d9-f35a15d98687.0.5.15"),subQ0])],"isStart":false})}),makeQuery(id+"F7.opExtrude","SWEPT_FACE",FACE,{"disambiguationData":[OSD([sQuery(id+"F4.wireOp",EDGE,"E27")])]})]});}
            chamfer(context, id + "F8", {"entities" : qUnion([Q0]), "width" : 5 * mm, "tangentPropagation" : true});
        }
        {
            var Q0;
            Q0=qCreatedBy(makeId("Front.planeOp"),FACE);
            var sketch = newSketch(context, id + "F9", { "sketchPlane" : qUnion([Q0])});
            skCircle(sketch, "E30", {"center": v(-39.88, 9.5) * mm, "radius": 3.75 * mm});
            skCircle(sketch, "E31.0.1.0", {"center": v(-39.88, 20.75) * mm, "radius": 3.75 * mm});
            skCircle(sketch, "E31.0.2.0", {"center": v(-39.88, 32) * mm, "radius": 3.75 * mm});
            skCircle(sketch, "E31.0.3.0", {"center": v(-39.88, 43.25) * mm, "radius": 3.75 * mm});
            skCircle(sketch, "E31.0.4.0", {"center": v(-39.88, 54.5) * mm, "radius": 3.75 * mm});
            skCircle(sketch, "E31.1.0.0", {"center": v(-28.63, 9.5) * mm, "radius": 3.75 * mm});
            skCircle(sketch, "E31.1.1.0", {"center": v(-28.63, 20.75) * mm, "radius": 3.75 * mm});
            skCircle(sketch, "E31.1.2.0", {"center": v(-28.63, 32) * mm, "radius": 3.75 * mm});
            skCircle(sketch, "E31.1.3.0", {"center": v(-28.63, 43.25) * mm, "radius": 3.75 * mm});
            skCircle(sketch, "E31.1.4.0", {"center": v(-28.63, 54.5) * mm, "radius": 3.75 * mm});
            skCircle(sketch, "E31.2.0.0", {"center": v(-17.38, 9.5) * mm, "radius": 3.75 * mm});
            skCircle(sketch, "E31.2.1.0", {"center": v(-17.38, 20.75) * mm, "radius": 3.75 * mm});
            skCircle(sketch, "E31.2.2.0", {"center": v(-17.38, 32) * mm, "radius": 3.75 * mm});
            skCircle(sketch, "E31.2.3.0", {"center": v(-17.38, 43.25) * mm, "radius": 3.75 * mm});
            skCircle(sketch, "E31.2.4.0", {"center": v(-17.38, 54.5) * mm, "radius": 3.75 * mm});
            skCircle(sketch, "E31.3.0.0", {"center": v(-6.13, 9.5) * mm, "radius": 3.75 * mm});
            skCircle(sketch, "E31.3.1.0", {"center": v(-6.13, 20.75) * mm, "radius": 3.75 * mm});
            skCircle(sketch, "E31.3.2.0", {"center": v(-6.13, 32) * mm, "radius": 3.75 * mm});
            skCircle(sketch, "E31.3.3.0", {"center": v(-6.13, 43.25) * mm, "radius": 3.75 * mm});
            skCircle(sketch, "E31.3.4.0", {"center": v(-6.13, 54.5) * mm, "radius": 3.75 * mm});
            skCircle(sketch, "E31.4.0.0", {"center": v(5.12, 9.5) * mm, "radius": 3.75 * mm});
            skCircle(sketch, "E31.4.1.0", {"center": v(5.12, 20.75) * mm, "radius": 3.75 * mm});
            skCircle(sketch, "E31.4.2.0", {"center": v(5.12, 32) * mm, "radius": 3.75 * mm});
            skCircle(sketch, "E31.4.3.0", {"center": v(5.12, 43.25) * mm, "radius": 3.75 * mm});
            skCircle(sketch, "E31.4.4.0", {"center": v(5.12, 54.5) * mm, "radius": 3.75 * mm});
            skCircle(sketch, "E31.5.0.0", {"center": v(16.37, 9.5) * mm, "radius": 3.75 * mm});
            skCircle(sketch, "E31.5.1.0", {"center": v(16.37, 20.75) * mm, "radius": 3.75 * mm});
            skCircle(sketch, "E31.5.2.0", {"center": v(16.37, 32) * mm, "radius": 3.75 * mm});
            skCircle(sketch, "E31.5.3.0", {"center": v(16.37, 43.25) * mm, "radius": 3.75 * mm});
            skCircle(sketch, "E31.5.4.0", {"center": v(16.37, 54.5) * mm, "radius": 3.75 * mm});
            skCircle(sketch, "E31.6.0.0", {"center": v(27.62, 9.5) * mm, "radius": 3.75 * mm});
            skCircle(sketch, "E31.6.1.0", {"center": v(27.62, 20.75) * mm, "radius": 3.75 * mm});
            skCircle(sketch, "E31.6.2.0", {"center": v(27.62, 32) * mm, "radius": 3.75 * mm});
            skCircle(sketch, "E31.6.3.0", {"center": v(27.62, 43.25) * mm, "radius": 3.75 * mm});
            skCircle(sketch, "E31.6.4.0", {"center": v(27.62, 54.5) * mm, "radius": 3.75 * mm});
            skCircle(sketch, "E31.7.0.0", {"center": v(38.87, 9.5) * mm, "radius": 3.75 * mm});
            skCircle(sketch, "E31.7.1.0", {"center": v(38.87, 20.75) * mm, "radius": 3.75 * mm});
            skCircle(sketch, "E31.7.2.0", {"center": v(38.87, 32) * mm, "radius": 3.75 * mm});
            skCircle(sketch, "E31.7.3.0", {"center": v(38.87, 43.25) * mm, "radius": 3.75 * mm});
            skCircle(sketch, "E31.7.4.0", {"center": v(38.87, 54.5) * mm, "radius": 3.75 * mm});
            skLineSegment(sketch, "E31.direction1", {"start": v(-39.88, 9.5) * mm, "end": v(-28.63, 9.5) * mm, "construction": true});
            skLineSegment(sketch, "E31.direction2", {"start": v(-39.88, 9.5) * mm, "end": v(-39.88, 20.75) * mm, "construction": true});
            skSolve(sketch);
        }
        {
            var Q0;
            Q0 = qSketchRegion(id + "F9", true);
            extrude(context, id + "F10", {"entities" : qUnion([Q0]), "operationType" : NewBodyOperationType.REMOVE, "endBound" : BoundingType.THROUGH_ALL, "oppositeDirection" : true, "depth" : 25 * mm, "offsetDistance" : 25 * mm, "hasSecondDirection" : true, "secondDirectionBound" : SecondDirectionBoundingType.THROUGH_ALL, "secondDirectionOppositeDirection" : false, "secondDirectionDepth" : 25 * mm});
        }
        {
            var Q0;
            Q0=qCreatedBy(makeId("Right.planeOp"),FACE);
            var sketch = newSketch(context, id + "F11", { "sketchPlane" : qUnion([Q0])});
            skLineSegment(sketch, "E32.0", {"start": v(174.82, 67) * mm, "end": v(-20.18, 67) * mm});
            skLineSegment(sketch, "E33.0", {"start": v(-5.55, 67) * mm, "end": v(-5.55, 2) * mm});
            skLineSegment(sketch, "E34.0", {"start": v(-20.18, 67) * mm, "end": v(-20.18, 0) * mm});
            skLineSegment(sketch, "E35", {"start": v(-5.55, 2) * mm, "end": v(-20.18, 2) * mm});
            skLineSegment(sketch, "E36", {"start": v(-5.55, 63) * mm, "end": v(-20.18, 63) * mm});
            skLineSegment(sketch, "E37", {"start": v(-20.18, 59) * mm, "end": v(-5.55, 44.38) * mm});
            skCircle(sketch, "E38", {"center": v(-11.18, 57.38) * mm, "radius": 3.75 * mm});
            skCircle(sketch, "E39", {"center": v(167.32, 7.5) * mm, "radius": 3.75 * mm});
            skCircle(sketch, "E40.0.1.0", {"center": v(167.32, 18.75) * mm, "radius": 3.75 * mm});
            skCircle(sketch, "E40.0.2.0", {"center": v(167.32, 30) * mm, "radius": 3.75 * mm});
            skCircle(sketch, "E40.0.3.0", {"center": v(167.32, 41.25) * mm, "radius": 3.75 * mm});
            skCircle(sketch, "E40.0.4.0", {"center": v(167.32, 52.5) * mm, "radius": 3.75 * mm});
            skLineSegment(sketch, "E40.direction1", {"start": v(167.32, 7.5) * mm, "end": v(156.07, 7.5) * mm, "construction": true});
            skLineSegment(sketch, "E40.direction2", {"start": v(167.32, 7.5) * mm, "end": v(167.32, 18.75) * mm, "construction": true});
            skLineSegment(sketch, "E41", {"start": v(-20.18, 61) * mm, "end": v(-20.18, 2) * mm});
            skLineSegment(sketch, "E42", {"start": v(-5.55, 44.38) * mm, "end": v(-5.55, 2) * mm});
            skSolve(sketch);
        }
        {
            var Q0;
            Q0=makeQuery(id+"F11.imprint","IMPRINT",FACE,{"disambiguationData":[TD([[makeQuery(id+"F11.imprint","IMPRINT",EDGE,{"derivedFrom":sQuery(id+"F11.wireOp",EDGE,"E37")}),-1.0]])]});
            var Q1;
            Q1=makeQuery(id+"F11.imprint","IMPRINT",FACE,{"disambiguationData":[TD([[makeQuery(id+"F11.imprint","IMPRINT",EDGE,{"derivedFrom":sQuery(id+"F11.wireOp",EDGE,"E40.0.4.0")}),1.0]])]});
            var Q2;
            Q2=makeQuery(id+"F11.imprint","IMPRINT",FACE,{"disambiguationData":[TD([[makeQuery(id+"F11.imprint","IMPRINT",EDGE,{"derivedFrom":sQuery(id+"F11.wireOp",EDGE,"E40.1.4.0")}),1.0]])]});
            var Q3;
            Q3=makeQuery(id+"F11.imprint","IMPRINT",FACE,{"disambiguationData":[TD([[makeQuery(id+"F11.imprint","IMPRINT",EDGE,{"derivedFrom":sQuery(id+"F11.wireOp",EDGE,"E40.0.3.0")}),1.0]])]});
            var Q4;
            Q4=makeQuery(id+"F11.imprint","IMPRINT",FACE,{"disambiguationData":[TD([[makeQuery(id+"F11.imprint","IMPRINT",EDGE,{"derivedFrom":sQuery(id+"F11.wireOp",EDGE,"E40.1.3.0")}),1.0]])]});
            var Q5;
            Q5=makeQuery(id+"F11.imprint","IMPRINT",FACE,{"disambiguationData":[TD([[makeQuery(id+"F11.imprint","IMPRINT",EDGE,{"derivedFrom":sQuery(id+"F11.wireOp",EDGE,"E40.2.3.0")}),1.0]])]});
            var Q6;
            Q6=makeQuery(id+"F11.imprint","IMPRINT",FACE,{"disambiguationData":[TD([[makeQuery(id+"F11.imprint","IMPRINT",EDGE,{"derivedFrom":sQuery(id+"F11.wireOp",EDGE,"E40.2.4.0")}),1.0]])]});
            var Q7;
            Q7=makeQuery(id+"F11.imprint","IMPRINT",FACE,{"disambiguationData":[TD([[makeQuery(id+"F11.imprint","IMPRINT",EDGE,{"derivedFrom":sQuery(id+"F11.wireOp",EDGE,"E40.3.4.0")}),1.0]])]});
            var Q8;
            Q8=makeQuery(id+"F11.imprint","IMPRINT",FACE,{"disambiguationData":[TD([[makeQuery(id+"F11.imprint","IMPRINT",EDGE,{"derivedFrom":sQuery(id+"F11.wireOp",EDGE,"E40.4.4.0")}),1.0]])]});
            var Q9;
            Q9=makeQuery(id+"F11.imprint","IMPRINT",FACE,{"disambiguationData":[TD([[makeQuery(id+"F11.imprint","IMPRINT",EDGE,{"derivedFrom":sQuery(id+"F11.wireOp",EDGE,"E40.3.3.0")}),1.0]])]});
            var Q10;
            Q10=makeQuery(id+"F11.imprint","IMPRINT",FACE,{"disambiguationData":[TD([[makeQuery(id+"F11.imprint","IMPRINT",EDGE,{"derivedFrom":sQuery(id+"F11.wireOp",EDGE,"E40.4.3.0")}),1.0]])]});
            var Q11;
            Q11=makeQuery(id+"F11.imprint","IMPRINT",FACE,{"disambiguationData":[TD([[makeQuery(id+"F11.imprint","IMPRINT",EDGE,{"derivedFrom":sQuery(id+"F11.wireOp",EDGE,"E40.3.2.0")}),1.0]])]});
            var Q12;
            Q12=makeQuery(id+"F11.imprint","IMPRINT",FACE,{"disambiguationData":[TD([[makeQuery(id+"F11.imprint","IMPRINT",EDGE,{"derivedFrom":sQuery(id+"F11.wireOp",EDGE,"E40.4.2.0")}),1.0]])]});
            var Q13;
            Q13=makeQuery(id+"F11.imprint","IMPRINT",FACE,{"disambiguationData":[TD([[makeQuery(id+"F11.imprint","IMPRINT",EDGE,{"derivedFrom":sQuery(id+"F11.wireOp",EDGE,"E40.2.2.0")}),1.0]])]});
            var Q14;
            Q14=makeQuery(id+"F11.imprint","IMPRINT",FACE,{"disambiguationData":[TD([[makeQuery(id+"F11.imprint","IMPRINT",EDGE,{"derivedFrom":sQuery(id+"F11.wireOp",EDGE,"E40.1.2.0")}),1.0]])]});
            var Q15;
            Q15=makeQuery(id+"F11.imprint","IMPRINT",FACE,{"disambiguationData":[TD([[makeQuery(id+"F11.imprint","IMPRINT",EDGE,{"derivedFrom":sQuery(id+"F11.wireOp",EDGE,"E40.0.2.0")}),1.0]])]});
            var Q16;
            Q16=makeQuery(id+"F11.imprint","IMPRINT",FACE,{"disambiguationData":[TD([[makeQuery(id+"F11.imprint","IMPRINT",EDGE,{"derivedFrom":sQuery(id+"F11.wireOp",EDGE,"E40.0.1.0")}),1.0]])]});
            var Q17;
            Q17=makeQuery(id+"F11.imprint","IMPRINT",FACE,{"disambiguationData":[TD([[makeQuery(id+"F11.imprint","IMPRINT",EDGE,{"derivedFrom":sQuery(id+"F11.wireOp",EDGE,"E40.1.1.0")}),1.0]])]});
            var Q18;
            Q18=makeQuery(id+"F11.imprint","IMPRINT",FACE,{"disambiguationData":[TD([[makeQuery(id+"F11.imprint","IMPRINT",EDGE,{"derivedFrom":sQuery(id+"F11.wireOp",EDGE,"E40.2.1.0")}),1.0]])]});
            var Q19;
            Q19=makeQuery(id+"F11.imprint","IMPRINT",FACE,{"disambiguationData":[TD([[makeQuery(id+"F11.imprint","IMPRINT",EDGE,{"derivedFrom":sQuery(id+"F11.wireOp",EDGE,"E40.3.1.0")}),1.0]])]});
            var Q20;
            Q20=makeQuery(id+"F11.imprint","IMPRINT",FACE,{"disambiguationData":[TD([[makeQuery(id+"F11.imprint","IMPRINT",EDGE,{"derivedFrom":sQuery(id+"F11.wireOp",EDGE,"E40.4.1.0")}),1.0]])]});
            var Q21;
            Q21=makeQuery(id+"F11.imprint","IMPRINT",FACE,{"disambiguationData":[TD([[makeQuery(id+"F11.imprint","IMPRINT",EDGE,{"derivedFrom":sQuery(id+"F11.wireOp",EDGE,"E40.3.0.0")}),1.0]])]});
            var Q22;
            Q22=makeQuery(id+"F11.imprint","IMPRINT",FACE,{"disambiguationData":[TD([[makeQuery(id+"F11.imprint","IMPRINT",EDGE,{"derivedFrom":sQuery(id+"F11.wireOp",EDGE,"E40.4.0.0")}),1.0]])]});
            var Q23;
            Q23=makeQuery(id+"F11.imprint","IMPRINT",FACE,{"disambiguationData":[TD([[makeQuery(id+"F11.imprint","IMPRINT",EDGE,{"derivedFrom":sQuery(id+"F11.wireOp",EDGE,"E40.2.0.0")}),1.0]])]});
            var Q24;
            Q24=makeQuery(id+"F11.imprint","IMPRINT",FACE,{"disambiguationData":[TD([[makeQuery(id+"F11.imprint","IMPRINT",EDGE,{"derivedFrom":sQuery(id+"F11.wireOp",EDGE,"E40.1.0.0")}),1.0]])]});
            var Q25;
            Q25=makeQuery(id+"F11.imprint","IMPRINT",FACE,{"disambiguationData":[TD([[makeQuery(id+"F11.imprint","IMPRINT",EDGE,{"derivedFrom":sQuery(id+"F11.wireOp",EDGE,"E39")}),1.0]])]});
            var Q26;
            Q26=makeQuery(id+"F11.imprint","IMPRINT",FACE,{"disambiguationData":[TD([[makeQuery(id+"F11.imprint","IMPRINT",EDGE,{"derivedFrom":sQuery(id+"F11.wireOp",EDGE,"E38")}),1.0]])]});
            extrude(context, id + "F12", {"entities" : qUnion([Q0, Q1, Q2, Q3, Q4, Q5, Q6, Q7, Q8, Q9, Q10, Q11, Q12, Q13, Q14, Q15, Q16, Q17, Q18, Q19, Q20, Q21, Q22, Q23, Q24, Q25, Q26]), "operationType" : NewBodyOperationType.REMOVE, "endBound" : BoundingType.THROUGH_ALL, "oppositeDirection" : true, "depth" : 25 * mm, "offsetDistance" : 25 * mm, "hasSecondDirection" : true, "secondDirectionBound" : SecondDirectionBoundingType.THROUGH_ALL, "secondDirectionOppositeDirection" : false, "secondDirectionDepth" : 25 * mm});
        }
        {
            var Q0;
            {var subQ0=sQuery(id+"F4.wireOp",EDGE,"E11.MirrorCS");Q0=makeQuery(id+"F6.boolean.opBoolean","INTERSECT",EDGE,{"derivedFrom":[makeQuery(id+"F5.opExtrude","CAP_FACE",FACE,{"disambiguationData":[OSD([sQuery(id+"F4.wireOp",EDGE,"E0.top"),sQuery(id+"F4.wireOp",EDGE,"E0.right"),sQuery(id+"F4.wireOp",EDGE,"E2.left"),sQuery(id+"F4.wireOp",EDGE,"E2.right"),sQuery(id+"F4.wireOp",EDGE,"E3.top"),sQuery(id+"F4.wireOp",EDGE,"E6.MirrorCS"),sQuery(id+"F4.wireOp",EDGE,"E7.MirrorCS"),subQ0,sQuery(id+"F4.wireOp",EDGE,"E13.MirrorCS"),sQuery(id+"F4.wireOp",EDGE,"E15.MirrorCS"),sQuery(id+"F4.wireOp",EDGE,"E16.MirrorCS"),sQuery(id+"F4.wireOp",EDGE,"E25"),sQuery(id+"F4.wireOp",EDGE,"E26.top"),sQuery(id+"F4.wireOp",EDGE,"E26.left"),sQuery(id+"F4.wireOp",EDGE,"E26.right")])],"isStart":false}),makeQuery(id+"F6.opExtrude","SWEPT_FACE",FACE,{"disambiguationData":[OSD([subQ0])]})]});}
            var Q1;
            {var subQ0=sQuery(id+"F4.wireOp",EDGE,"E2.right");Q1=makeQuery(id+"F6.boolean.opBoolean","INTERSECT",EDGE,{"derivedFrom":[makeQuery(id+"F5.opExtrude","CAP_FACE",FACE,{"disambiguationData":[OSD([sQuery(id+"F4.wireOp",EDGE,"E0.top"),sQuery(id+"F4.wireOp",EDGE,"E0.right"),sQuery(id+"F4.wireOp",EDGE,"E2.left"),subQ0,sQuery(id+"F4.wireOp",EDGE,"E3.top"),sQuery(id+"F4.wireOp",EDGE,"E6.MirrorCS"),sQuery(id+"F4.wireOp",EDGE,"E7.MirrorCS"),sQuery(id+"F4.wireOp",EDGE,"E11.MirrorCS"),sQuery(id+"F4.wireOp",EDGE,"E13.MirrorCS"),sQuery(id+"F4.wireOp",EDGE,"E15.MirrorCS"),sQuery(id+"F4.wireOp",EDGE,"E16.MirrorCS"),sQuery(id+"F4.wireOp",EDGE,"E25"),sQuery(id+"F4.wireOp",EDGE,"E26.top"),sQuery(id+"F4.wireOp",EDGE,"E26.left"),sQuery(id+"F4.wireOp",EDGE,"E26.right")])],"isStart":false}),makeQuery(id+"F6.opExtrude","SWEPT_FACE",FACE,{"disambiguationData":[OSD([subQ0])]})]});}
            var Q2;
            Q2=makeQuery(id+"F5.opExtrude","CAP_EDGE",EDGE,{"disambiguationData":[OSD([sQuery(id+"F4.wireOp",EDGE,"E22.trimOffspring")])],"isStart":false});
            var Q3;
            Q3=makeQuery(id+"F6.opExtrude","SWEPT_EDGE",EDGE,{"disambiguationData":[OSD([sQuery(id+"F4.wireOp",EDGE,"E14.MirrorCS"),sQuery(id+"F4.wireOp",EDGE,"E22.trimOffspring")])]});
            var Q4;
            Q4=makeQuery(id+"F6.opExtrude","SWEPT_EDGE",EDGE,{"disambiguationData":[OSD([sQuery(id+"F4.wireOp",EDGE,"E3.bottom"),sQuery(id+"F4.wireOp",EDGE,"E21.trimOffspring")])]});
            var Q5;
            Q5=makeQuery(id+"F5.opExtrude","CAP_EDGE",EDGE,{"disambiguationData":[OSD([sQuery(id+"F4.wireOp",EDGE,"E10.MirrorCS")])],"isStart":false});
            var Q6;
            {var subQ0=sQuery(id+"F4.wireOp",EDGE,"E12.MirrorCS");Q6=makeQuery(id+"F5.opExtrude","CAP_EDGE",EDGE,{"disambiguationData":[OSD([subQ0]),TDD([makeQuery(id+"F4.imprint","IMPRINT",EDGE,{"disambiguationData":[TD([[makeQuery(id+"F4.imprint","INTERSECT",VERTEX,{"disambiguationData":[OD(1.0)],"derivedFrom":[subQ0,sQuery(id+"F4.wireOp",EDGE,"b3370406-a8f8-48eb-b0d9-f35a15d98687.0.1.16")]}),-1.0]])],"derivedFrom":subQ0})])],"isStart":false});}
            var Q7;
            {var subQ0=sQuery(id+"F4.wireOp",EDGE,"E12.MirrorCS");Q7=makeQuery(id+"F5.opExtrude","CAP_EDGE",EDGE,{"disambiguationData":[OSD([subQ0]),TDD([makeQuery(id+"F4.imprint","IMPRINT",EDGE,{"disambiguationData":[TD([[makeQuery(id+"F4.imprint","INTERSECT",VERTEX,{"derivedFrom":[sQuery(id+"F4.wireOp",EDGE,"E10.MirrorCS"),subQ0]}),1.0]])],"derivedFrom":subQ0})])],"isStart":false});}
            var Q8;
            {var subQ0=sQuery(id+"F4.wireOp",EDGE,"E12.MirrorCS");Q8=makeQuery(id+"F5.opExtrude","CAP_EDGE",EDGE,{"disambiguationData":[OSD([subQ0]),TDD([makeQuery(id+"F4.imprint","IMPRINT",EDGE,{"disambiguationData":[TD([[makeQuery(id+"F4.imprint","INTERSECT",VERTEX,{"disambiguationData":[OD(1.0)],"derivedFrom":[subQ0,sQuery(id+"F4.wireOp",EDGE,"b3370406-a8f8-48eb-b0d9-f35a15d98687.0.2.16")]}),-1.0]])],"derivedFrom":subQ0})])],"isStart":false});}
            var Q9;
            Q9=makeQuery(id+"F5.opExtrude","CAP_EDGE",EDGE,{"disambiguationData":[OSD([sQuery(id+"F4.wireOp",EDGE,"E5.top"),sQuery(id+"F4.wireOp",EDGE,"E12.MirrorCS")])],"isStart":false});
            var Q10;
            {var subQ0=sQuery(id+"F4.wireOp",EDGE,"E5.top");Q10=makeQuery(id+"F5.opExtrude","CAP_EDGE",EDGE,{"disambiguationData":[OSD([subQ0]),TDD([makeQuery(id+"F4.imprint","IMPRINT",EDGE,{"disambiguationData":[TD([[makeQuery(id+"F4.imprint","INTERSECT",VERTEX,{"disambiguationData":[OD(1.0)],"derivedFrom":[subQ0,sQuery(id+"F4.wireOp",EDGE,"b3370406-a8f8-48eb-b0d9-f35a15d98687.0.3.16")]}),-1.0]])],"derivedFrom":subQ0})])],"isStart":false});}
            var Q11;
            {var subQ0=sQuery(id+"F4.wireOp",EDGE,"E5.top");Q11=makeQuery(id+"F5.opExtrude","CAP_EDGE",EDGE,{"disambiguationData":[OSD([subQ0]),TDD([makeQuery(id+"F4.imprint","IMPRINT",EDGE,{"disambiguationData":[TD([[makeQuery(id+"F4.imprint","INTERSECT",VERTEX,{"disambiguationData":[OD(1.0)],"derivedFrom":[subQ0,sQuery(id+"F4.wireOp",EDGE,"b3370406-a8f8-48eb-b0d9-f35a15d98687.0.4.16")]}),-1.0]])],"derivedFrom":subQ0})])],"isStart":false});}
            var Q12;
            {var subQ0=sQuery(id+"F4.wireOp",EDGE,"E26.bottom");Q12=makeQuery(id+"F5.opExtrude","CAP_EDGE",EDGE,{"disambiguationData":[OSD([subQ0]),TDD([makeQuery(id+"F4.imprint","IMPRINT",EDGE,{"disambiguationData":[TD([[makeQuery(id+"F4.imprint","INTERSECT",VERTEX,{"disambiguationData":[OD(1.0)],"derivedFrom":[subQ0,sQuery(id+"F4.wireOp",EDGE,"b3370406-a8f8-48eb-b0d9-f35a15d98687.0.0.16")]}),-1.0]])],"derivedFrom":subQ0})])],"isStart":false});}
            var Q13;
            {var subQ0=sQuery(id+"F4.wireOp",EDGE,"E26.bottom");Q13=makeQuery(id+"F5.opExtrude","CAP_EDGE",EDGE,{"disambiguationData":[OSD([subQ0]),TDD([makeQuery(id+"F4.imprint","IMPRINT",EDGE,{"disambiguationData":[TD([[makeQuery(id+"F4.imprint","INTERSECT",VERTEX,{"disambiguationData":[OD(0.0)],"derivedFrom":[subQ0,sQuery(id+"F4.wireOp",EDGE,"b3370406-a8f8-48eb-b0d9-f35a15d98687.0.0.16")]}),1.0]])],"derivedFrom":subQ0})])],"isStart":false});}
            var Q14;
            {var subQ0=sQuery(id+"F4.wireOp",EDGE,"E26.bottom");Q14=makeQuery(id+"F5.opExtrude","CAP_EDGE",EDGE,{"disambiguationData":[OSD([subQ0]),TDD([makeQuery(id+"F4.imprint","IMPRINT",EDGE,{"disambiguationData":[TD([[makeQuery(id+"F4.imprint","INTERSECT",VERTEX,{"disambiguationData":[OD(1.0)],"derivedFrom":[subQ0,sQuery(id+"F4.wireOp",EDGE,"b3370406-a8f8-48eb-b0d9-f35a15d98687.0.1.16")]}),-1.0]])],"derivedFrom":subQ0})])],"isStart":false});}
            var Q15;
            {var subQ0=sQuery(id+"F4.wireOp",EDGE,"E26.bottom");Q15=makeQuery(id+"F5.opExtrude","CAP_EDGE",EDGE,{"disambiguationData":[OSD([subQ0]),TDD([makeQuery(id+"F4.imprint","IMPRINT",EDGE,{"disambiguationData":[TD([[makeQuery(id+"F4.imprint","INTERSECT",VERTEX,{"disambiguationData":[OD(1.0)],"derivedFrom":[subQ0,sQuery(id+"F4.wireOp",EDGE,"b3370406-a8f8-48eb-b0d9-f35a15d98687.0.2.16")]}),-1.0]])],"derivedFrom":subQ0})])],"isStart":false});}
            var Q16;
            {var subQ0=sQuery(id+"F4.wireOp",EDGE,"E26.bottom");Q16=makeQuery(id+"F5.opExtrude","CAP_EDGE",EDGE,{"disambiguationData":[OSD([subQ0]),TDD([makeQuery(id+"F4.imprint","IMPRINT",EDGE,{"disambiguationData":[TD([[makeQuery(id+"F4.imprint","INTERSECT",VERTEX,{"disambiguationData":[OD(1.0)],"derivedFrom":[subQ0,sQuery(id+"F4.wireOp",EDGE,"b3370406-a8f8-48eb-b0d9-f35a15d98687.0.3.16")]}),-1.0]])],"derivedFrom":subQ0})])],"isStart":false});}
            var Q17;
            {var subQ0=sQuery(id+"F4.wireOp",EDGE,"E26.bottom");Q17=makeQuery(id+"F5.opExtrude","CAP_EDGE",EDGE,{"disambiguationData":[OSD([subQ0]),TDD([makeQuery(id+"F4.imprint","IMPRINT",EDGE,{"disambiguationData":[TD([[makeQuery(id+"F4.imprint","INTERSECT",VERTEX,{"disambiguationData":[OD(1.0)],"derivedFrom":[subQ0,sQuery(id+"F4.wireOp",EDGE,"b3370406-a8f8-48eb-b0d9-f35a15d98687.0.4.16")]}),-1.0]])],"derivedFrom":subQ0})])],"isStart":false});}
            var Q18;
            Q18=makeQuery(id+"F6.opExtrude","SWEPT_EDGE",EDGE,{"disambiguationData":[OSD([sQuery(id+"F4.wireOp",EDGE,"E16.MirrorCS"),sQuery(id+"F4.wireOp",EDGE,"E26.bottom"),sQuery(id+"F4.wireOp",EDGE,"E26.left")])]});
            var Q19;
            Q19=makeQuery(id+"F6.opExtrude","SWEPT_EDGE",EDGE,{"disambiguationData":[OSD([sQuery(id+"F4.wireOp",EDGE,"E10.MirrorCS"),sQuery(id+"F4.wireOp",EDGE,"E12.MirrorCS")])]});
            var Q20;
            Q20=makeQuery(id+"F6.opExtrude","SWEPT_EDGE",EDGE,{"disambiguationData":[OSD([sQuery(id+"F4.wireOp",EDGE,"E1"),sQuery(id+"F4.wireOp",EDGE,"E5.top")])]});
            var Q21;
            Q21=makeQuery(id+"F6.opExtrude","SWEPT_EDGE",EDGE,{"disambiguationData":[OSD([sQuery(id+"F4.wireOp",EDGE,"E0.right"),sQuery(id+"F4.wireOp",EDGE,"E26.bottom"),sQuery(id+"F4.wireOp",EDGE,"E26.right")])]});
            var Q22;
            Q22=makeQuery(id+"F6.opExtrude","SWEPT_EDGE",EDGE,{"disambiguationData":[OSD([sQuery(id+"F4.wireOp",EDGE,"E18.MirrorCS"),sQuery(id+"F4.wireOp",EDGE,"E22.trimOffspring")])]});
            var Q23;
            Q23=makeQuery(id+"F6.opExtrude","SWEPT_EDGE",EDGE,{"disambiguationData":[OSD([sQuery(id+"F4.wireOp",EDGE,"E10.MirrorCS"),sQuery(id+"F4.wireOp",EDGE,"E17.MirrorCS")])]});
            var Q24;
            Q24=makeQuery(id+"F6.opExtrude","SWEPT_EDGE",EDGE,{"disambiguationData":[OSD([sQuery(id+"F4.wireOp",EDGE,"E4.top"),sQuery(id+"F4.wireOp",EDGE,"E21.trimOffspring")])]});
            var Q25;
            Q25=makeQuery(id+"F6.opExtrude","SWEPT_EDGE",EDGE,{"disambiguationData":[OSD([sQuery(id+"F4.wireOp",EDGE,"E1"),sQuery(id+"F4.wireOp",EDGE,"E4.bottom")])]});
            var Q26;
            {var subQ0=sQuery(id+"F4.wireOp",EDGE,"E17.MirrorCS");Q26=makeQuery(id+"F5.opExtrude","CAP_EDGE",EDGE,{"disambiguationData":[OSD([subQ0]),TDD([makeQuery(id+"F4.imprint","IMPRINT",EDGE,{"disambiguationData":[TD([[makeQuery(id+"F4.imprint","INTERSECT",VERTEX,{"disambiguationData":[OD(1.0)],"derivedFrom":[subQ0,sQuery(id+"F4.wireOp",EDGE,"913f8327-6014-45d2-8669-990423f078e8.2.6.0")]}),-1.0]])],"derivedFrom":subQ0})])],"isStart":false});}
            var Q27;
            {var subQ0=sQuery(id+"F4.wireOp",EDGE,"E17.MirrorCS");Q27=makeQuery(id+"F5.opExtrude","CAP_EDGE",EDGE,{"disambiguationData":[OSD([subQ0]),TDD([makeQuery(id+"F4.imprint","IMPRINT",EDGE,{"disambiguationData":[TD([[makeQuery(id+"F4.imprint","INTERSECT",VERTEX,{"disambiguationData":[OD(1.0)],"derivedFrom":[subQ0,sQuery(id+"F4.wireOp",EDGE,"913f8327-6014-45d2-8669-990423f078e8.1.6.0")]}),-1.0]])],"derivedFrom":subQ0})])],"isStart":false});}
            var Q28;
            {var subQ0=sQuery(id+"F4.wireOp",EDGE,"E17.MirrorCS");Q28=makeQuery(id+"F5.opExtrude","CAP_EDGE",EDGE,{"disambiguationData":[OSD([subQ0]),TDD([makeQuery(id+"F4.imprint","IMPRINT",EDGE,{"disambiguationData":[TD([[makeQuery(id+"F4.imprint","INTERSECT",VERTEX,{"derivedFrom":[sQuery(id+"F4.wireOp",EDGE,"E10.MirrorCS"),subQ0]}),1.0]])],"derivedFrom":subQ0})])],"isStart":false});}
            var Q29;
            Q29=makeQuery(id+"F6.opExtrude","SWEPT_EDGE",EDGE,{"disambiguationData":[OSD([sQuery(id+"F4.wireOp",EDGE,"E10.MirrorCS"),sQuery(id+"F4.wireOp",EDGE,"E28.bottom"),sQuery(id+"F4.wireOp",EDGE,"E28.left")])]});
            var Q30;
            Q30=makeQuery(id+"F6.opExtrude","SWEPT_EDGE",EDGE,{"disambiguationData":[OSD([sQuery(id+"F4.wireOp",EDGE,"E1"),sQuery(id+"F4.wireOp",EDGE,"E28.bottom"),sQuery(id+"F4.wireOp",EDGE,"E28.right")])]});
            var Q31;
            Q31=makeQuery(id+"F6.opExtrude","SWEPT_EDGE",EDGE,{"disambiguationData":[OSD([sQuery(id+"F4.wireOp",EDGE,"E10.MirrorCS"),sQuery(id+"F4.wireOp",EDGE,"E28.top"),sQuery(id+"F4.wireOp",EDGE,"E28.left")])]});
            var Q32;
            Q32=makeQuery(id+"F6.opExtrude","SWEPT_EDGE",EDGE,{"disambiguationData":[OSD([sQuery(id+"F4.wireOp",EDGE,"E1"),sQuery(id+"F4.wireOp",EDGE,"E28.top"),sQuery(id+"F4.wireOp",EDGE,"E28.right")])]});
            var Q33;
            Q33=makeQuery(id+"F6.opExtrude","SWEPT_EDGE",EDGE,{"disambiguationData":[OSD([sQuery(id+"F4.wireOp",EDGE,"E10.MirrorCS"),sQuery(id+"F4.wireOp",EDGE,"E29.top"),sQuery(id+"F4.wireOp",EDGE,"E29.left")])]});
            var Q34;
            Q34=makeQuery(id+"F6.opExtrude","SWEPT_EDGE",EDGE,{"disambiguationData":[OSD([sQuery(id+"F4.wireOp",EDGE,"E1"),sQuery(id+"F4.wireOp",EDGE,"E29.top"),sQuery(id+"F4.wireOp",EDGE,"E29.right")])]});
            var Q35;
            Q35=makeQuery(id+"F6.opExtrude","SWEPT_EDGE",EDGE,{"disambiguationData":[OSD([sQuery(id+"F4.wireOp",EDGE,"E1"),sQuery(id+"F4.wireOp",EDGE,"E29.bottom"),sQuery(id+"F4.wireOp",EDGE,"E29.right")])]});
            var Q36;
            Q36=makeQuery(id+"F6.opExtrude","SWEPT_EDGE",EDGE,{"disambiguationData":[OSD([sQuery(id+"F4.wireOp",EDGE,"E10.MirrorCS"),sQuery(id+"F4.wireOp",EDGE,"E29.bottom"),sQuery(id+"F4.wireOp",EDGE,"E29.left")])]});
            chamfer(context, id + "F13", {"entities" : qUnion([Q0, Q1, Q2, Q3, Q4, Q5, Q6, Q7, Q8, Q9, Q10, Q11, Q12, Q13, Q14, Q15, Q16, Q17, Q18, Q19, Q20, Q21, Q22, Q23, Q24, Q25, Q26, Q27, Q28, Q29, Q30, Q31, Q32, Q33, Q34, Q35, Q36]), "width" : (getVariable(context, 'wall')) * mm, "tangentPropagation" : true});
        }
    });
